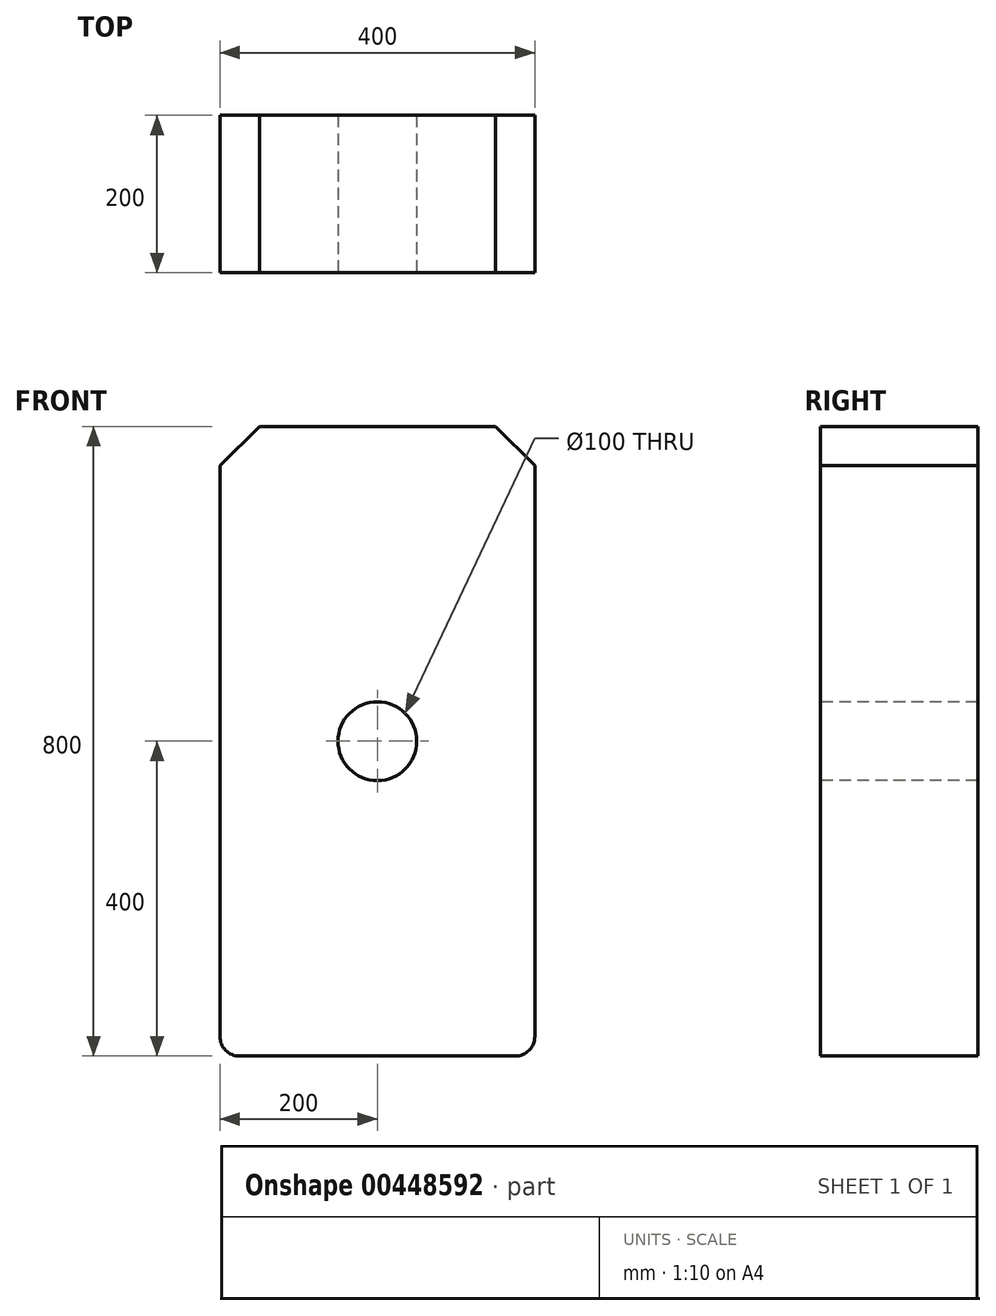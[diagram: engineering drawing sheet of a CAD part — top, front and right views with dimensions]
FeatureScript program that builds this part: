
annotation { "Feature Type Name" : "Feature", "Feature Type Description" : "" }
export const myFeature = defineFeature(function(context is Context, id is Id, definition is map)
    precondition{}
    {
        {
            var Q0;
            Q0=qCreatedBy(makeId("Front.planeOp"),FACE);
            var sketch = newSketch(context, id + "F0", { "sketchPlane" : qUnion([Q0])});
            skLineSegment(sketch, "E0.bottom", {"start": v(200, 400) * mm, "end": v(-200, 400) * mm});
            skLineSegment(sketch, "E0.top", {"start": v(200, -400) * mm, "end": v(-200, -400) * mm});
            skLineSegment(sketch, "E0.left", {"start": v(200, 400) * mm, "end": v(200, -400) * mm});
            skLineSegment(sketch, "E0.right", {"start": v(-200, 400) * mm, "end": v(-200, -400) * mm});
            skPoint(sketch, "E0.middle", {"position": v(0, 0) * mm});
            skSolve(sketch);
        }
        {
            var Q0;
            Q0 = qSketchRegion(id + "F0", true);
            extrude(context, id + "F1", {"entities" : qUnion([Q0]), "endBound" : BoundingType.SYMMETRIC, "depth" : 200 * mm});
        }
        {
            var Q0;
            Q0=makeQuery(id+"F1.opExtrude","SWEPT_EDGE",EDGE,{"disambiguationData":[OSD([sQuery(id+"F0.wireOp",EDGE,"E0.bottom"),sQuery(id+"F0.wireOp",EDGE,"E0.right")])]});
            var Q1;
            Q1=makeQuery(id+"F1.opExtrude","SWEPT_EDGE",EDGE,{"disambiguationData":[OSD([sQuery(id+"F0.wireOp",EDGE,"E0.bottom"),sQuery(id+"F0.wireOp",EDGE,"E0.left")])]});
            chamfer(context, id + "F2", {"entities" : qUnion([Q0, Q1]), "width" : 50 * mm, "tangentPropagation" : true});
        }
        {
            var Q0;
            Q0=makeQuery(id+"F1.opExtrude","SWEPT_EDGE",EDGE,{"disambiguationData":[OSD([sQuery(id+"F0.wireOp",EDGE,"E0.top"),sQuery(id+"F0.wireOp",EDGE,"E0.right")])]});
            var Q1;
            Q1=makeQuery(id+"F1.opExtrude","SWEPT_EDGE",EDGE,{"disambiguationData":[OSD([sQuery(id+"F0.wireOp",EDGE,"E0.top"),sQuery(id+"F0.wireOp",EDGE,"E0.left")])]});
            fillet(context, id + "F3", {"entities" : qUnion([Q0, Q1]), "radius" : 25 * mm, "tangentPropagation" : true, "allowEdgeOverflow" : false});
        }
        {
            var Q0;
            Q0=makeQuery(id+"F1.opExtrude","CAP_FACE",FACE,{"disambiguationData":[OSD([sQuery(id+"F0.wireOp",EDGE,"E0.bottom"),sQuery(id+"F0.wireOp",EDGE,"E0.top"),sQuery(id+"F0.wireOp",EDGE,"E0.left"),sQuery(id+"F0.wireOp",EDGE,"E0.right")])],"isStart":false});
            var sketch = newSketch(context, id + "F4", { "sketchPlane" : qUnion([Q0])});
            skCircle(sketch, "E1", {"center": v(0, 0) * mm, "radius": 50 * mm});
            skSolve(sketch);
        }
        {
            var Q0;
            Q0 = qSketchRegion(id + "F4", true);
            extrude(context, id + "F5", {"entities" : qUnion([Q0]), "operationType" : NewBodyOperationType.REMOVE, "oppositeDirection" : true, "depth" : 230 * mm});
        }
    });
